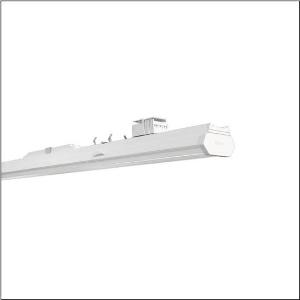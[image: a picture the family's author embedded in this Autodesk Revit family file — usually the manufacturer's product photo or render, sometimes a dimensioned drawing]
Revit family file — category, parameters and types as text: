
# Revit family: licross_r__11_protected_mo_51tp11cn49xg_312d
name_source: partatom
category: Lighting Fixtures
units: mm (PartAtom-declared; Revit-internal decimal feet)

## family parameters
Cut with Voids When Loaded = No
Host = Face
Light Source = No
Part Type = Normal
Room Calculation Point = No
Round Connector Dimension = Use Diameter
Shared = No

## types (1)
- --- (1 x LED, 9030 lm, 49.4 W, 4000K)
    Apparent Load = 49 VA
    CIE Flux Codes = 83 94 98 100 100
    Color Rendering = 80
    Color Temperature = 4000K
    Default Elevation = 1800 mm
    Description = Licross® 11 Protected MO, luminaire insert, of sheet steel, galvanised, coil coated, white, length: 1.500mm, width: 90mm, height: 101mm, LED rated luminous flux: 9.030lm, light colour: 840, control gear: ON/OFF Multilumen, CLOi, with plug, 3-pole, with phase selection, mains connection: 220..240V, AC, 50/60Hz, start of lifetime: 49W, end of service life: 55W, halogen-free wiring, primary light control with lens, of plastic, primary optical cover: cover, of PMMA, light emission: direct distribution, primary light characteristic: symmetric, protection rating (complete): IP64, insulation class (complete): insulation class I (protective earthing), certification: CE, ENEC, VDE, UKCA, protection symbol: D if used in an environment with conductive dust loads with corresponding accessories, impact resistance: IK06, permissible ambient temperature for indoor applications: -35..+40°C, corresponds to IFS (International Featured Standards) requirements for safety and quality in the food industry, reducing of maximum allowable ambient temperature of 5°C with ceiling mounting, LABS conformity tested according to VDMA 24364:2018-05, packaging unit: 1 piece
    Height = 92 mm
    Lamp = 1 x LED
    Lamp Light Flux = 9030 lm
    Lamp Power = 49.4 W
    Lamp count = 1
    Length = 1500 mm
    Luminous efficacy = 183 lm/W
    Manufacturer = Siteco
    ModVariant = No
    Model = 51TP11CN49XG
    Mounting Place = Ceiling
    Mounting Type = Pendant
    Number of Poles = 1
    OnlyDefault = Yes
    Power Factor = 1
    Product Name = Licross® 11 Protected MO
    Product group = luminaire insert
    ProductGroupID = 901
    Protection Class = Protection class I
    Protection Degree = IP 64
    RLX_Detail_Level = 1
    RLX_Emergency_Light_Flux = 0 lm
    RLX_Emergency_Type = 0
    RLX_Emergency_Type_DB = No
    RlxData = <blob elided: 21909 chars, md5=7828cc29>
    Socket = socket
    Standby Power = 0 W
    System Light Flux = 9030 lm
    System Power = 49 W
    Type Comments = factory setting: luminous flux: 100 % | (A | C | E) | 113 mA
    Type Image = l_1256148.jpg
    URL = http://relux.com
    VarID = @adj_037941
    Voltage = 0 V
    Weight = 0.00 kg
    Width = 88 mm

## geometry (parser evidence)
native form markers: Blend x4, Sweep x10
no freeform markers — native parametric forms only
